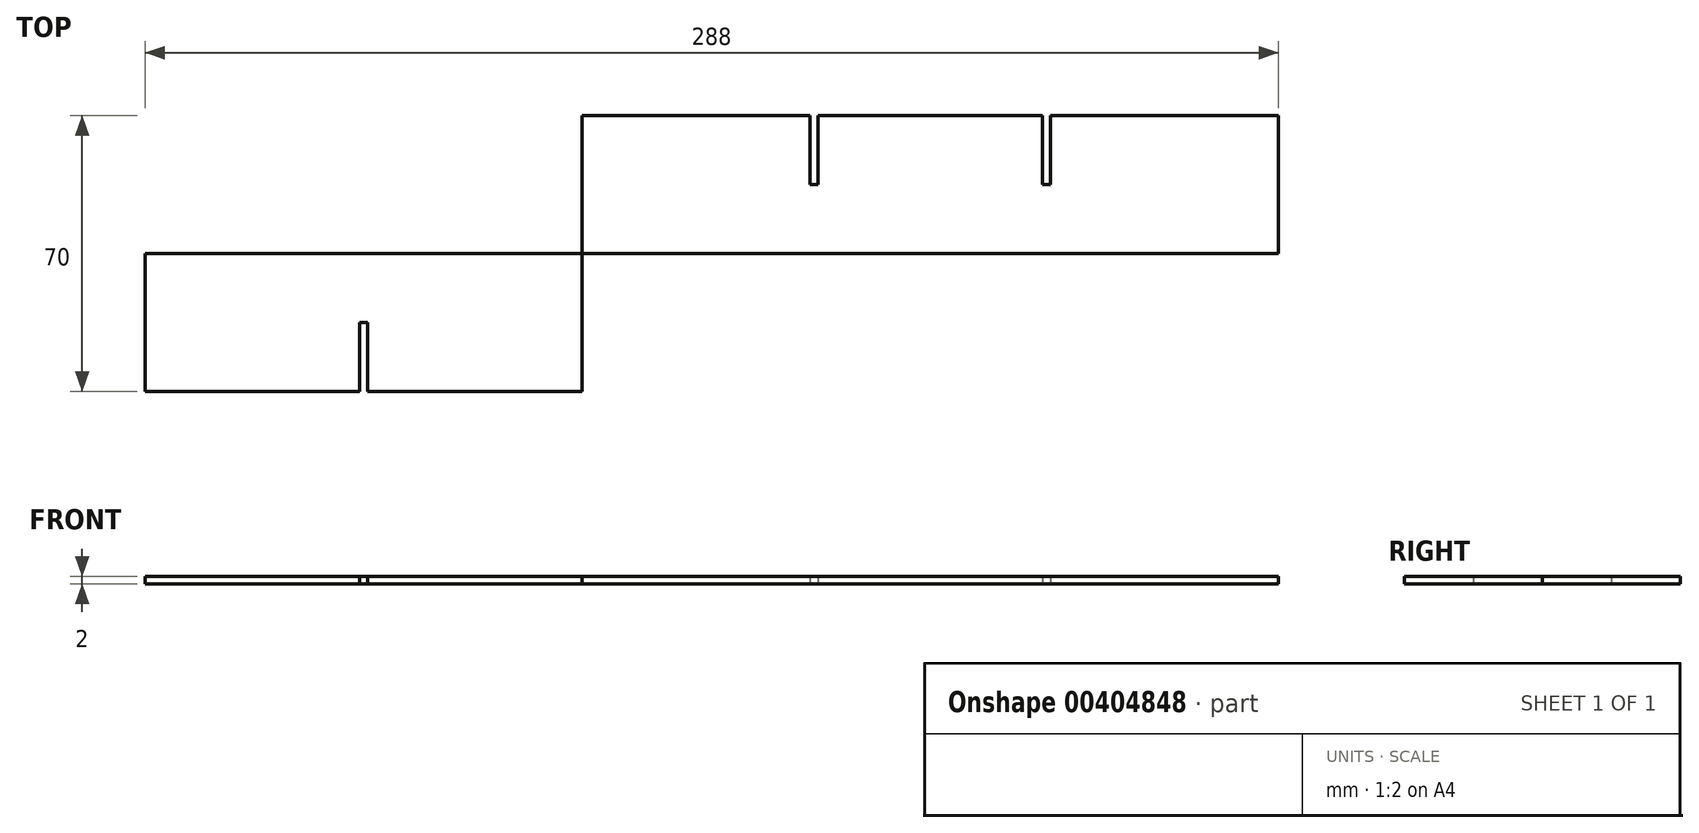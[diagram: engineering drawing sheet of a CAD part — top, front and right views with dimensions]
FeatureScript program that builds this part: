
annotation { "Feature Type Name" : "Feature", "Feature Type Description" : "" }
export const myFeature = defineFeature(function(context is Context, id is Id, definition is map)
    precondition{}
    {
        {
            var Q0;
            Q0=qCreatedBy(makeId("Top.planeOp"),FACE);
            var sketch = newSketch(context, id + "F0", { "sketchPlane" : qUnion([Q0])});
            skLineSegment(sketch, "E0.bottom", {"start": v(0, 0) * mm, "end": v(177, 0) * mm});
            skLineSegment(sketch, "E0.top", {"start": v(0, 35) * mm, "end": v(177, 35) * mm});
            skLineSegment(sketch, "E0.left", {"start": v(0, 0) * mm, "end": v(0, 35) * mm});
            skLineSegment(sketch, "E0.right", {"start": v(177, 0) * mm, "end": v(177, 35) * mm});
            skLineSegment(sketch, "E1", {"start": v(0, 17.5) * mm, "end": v(177, 17.5) * mm, "construction": true});
            skLineSegment(sketch, "E2", {"start": v(59, 35) * mm, "end": v(59, 17.5) * mm, "construction": true});
            skLineSegment(sketch, "E3", {"start": v(118, 35) * mm, "end": v(118, 17.5) * mm, "construction": true});
            skLineSegment(sketch, "E4.bottom", {"start": v(60, 17.5) * mm, "end": v(58, 17.5) * mm});
            skLineSegment(sketch, "E4.top", {"start": v(60, 52.5) * mm, "end": v(58, 52.5) * mm});
            skLineSegment(sketch, "E4.left", {"start": v(60, 17.5) * mm, "end": v(60, 52.5) * mm});
            skLineSegment(sketch, "E4.right", {"start": v(58, 17.5) * mm, "end": v(58, 52.5) * mm});
            skPoint(sketch, "E4.middle", {"position": v(59, 35) * mm});
            skLineSegment(sketch, "E5.bottom", {"start": v(119, 17.5) * mm, "end": v(117, 17.5) * mm});
            skLineSegment(sketch, "E5.top", {"start": v(119, 52.5) * mm, "end": v(117, 52.5) * mm});
            skLineSegment(sketch, "E5.left", {"start": v(119, 17.5) * mm, "end": v(119, 52.5) * mm});
            skLineSegment(sketch, "E5.right", {"start": v(117, 17.5) * mm, "end": v(117, 52.5) * mm});
            skPoint(sketch, "E5.middle", {"position": v(118, 35) * mm});
            skSolve(sketch);
        }
        {
            var Q0;
            Q0=qCreatedBy(makeId("Top.planeOp"),FACE);
            var sketch = newSketch(context, id + "F1", { "sketchPlane" : qUnion([Q0])});
            skLineSegment(sketch, "E6.bottom", {"start": v(0, 0) * mm, "end": v(-111, 0) * mm});
            skLineSegment(sketch, "E6.top", {"start": v(0, -35) * mm, "end": v(-111, -35) * mm});
            skLineSegment(sketch, "E6.left", {"start": v(0, 0) * mm, "end": v(0, -35) * mm});
            skLineSegment(sketch, "E6.right", {"start": v(-111, 0) * mm, "end": v(-111, -35) * mm});
            skLineSegment(sketch, "E7", {"start": v(-55.5, -35) * mm, "end": v(-55.5, 0) * mm, "construction": true});
            skLineSegment(sketch, "E8", {"start": v(-111, -17.5) * mm, "end": v(0, -17.5) * mm, "construction": true});
            skLineSegment(sketch, "E9.bottom", {"start": v(-54.5, -17.5) * mm, "end": v(-56.5, -17.5) * mm});
            skLineSegment(sketch, "E9.top", {"start": v(-54.5, -52.5) * mm, "end": v(-56.5, -52.5) * mm});
            skLineSegment(sketch, "E9.left", {"start": v(-54.5, -17.5) * mm, "end": v(-54.5, -52.5) * mm});
            skLineSegment(sketch, "E9.right", {"start": v(-56.5, -17.5) * mm, "end": v(-56.5, -52.5) * mm});
            skPoint(sketch, "E9.middle", {"position": v(-55.5, -35) * mm});
            skSolve(sketch);
        }
        {
            var Q0;
            Q0=makeQuery(id+"F0.imprint","IMPRINT",FACE,{"disambiguationData":[TD([[makeQuery(id+"F0.imprint","IMPRINT",EDGE,{"derivedFrom":sQuery(id+"F0.wireOp",EDGE,"E0.bottom")}),1.0]])]});
            extrude(context, id + "F2", {"entities" : qUnion([Q0]), "depth" : 2 * mm});
        }
        {
            var Q0;
            Q0=makeQuery(id+"F1.imprint","IMPRINT",FACE,{"disambiguationData":[TD([[makeQuery(id+"F1.imprint","IMPRINT",EDGE,{"derivedFrom":sQuery(id+"F1.wireOp",EDGE,"E6.bottom")}),1.0]])]});
            extrude(context, id + "F3", {"entities" : qUnion([Q0]), "depth" : 2 * mm});
        }
    });
